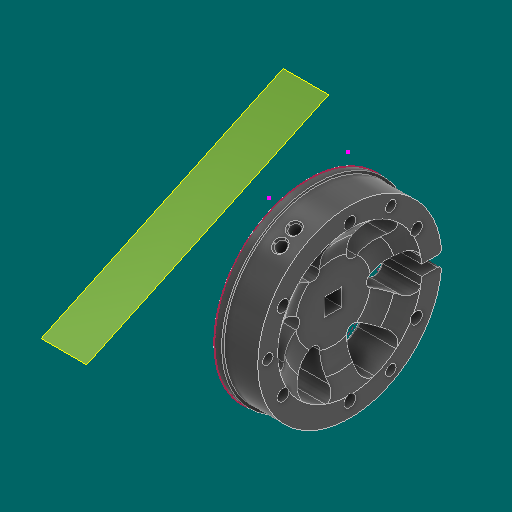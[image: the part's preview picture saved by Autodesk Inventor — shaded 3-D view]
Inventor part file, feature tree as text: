
AUTODESK INVENTOR PART (.ipt)
format: ipt  version: 2023.1 (Build 271208000, 208)  size: 545,792 bytes
history: native  units: in
note: dims shown in document units (in); Inventor stores cm internally (conversion verified against a paired STEP export)
features: sketch x7, other x4, plane x1
ambient origin geometry x8: Origin, YZ Plane, XZ Plane, XY Plane, X Axis, Y Axis, Z Axis, Center Point
bodies: Solid1 (feature_tree)
feature tree (12):
  other  "WheelHalf.ipt"
  other  "Solid1::WheelHalf.ipt"
  other  "TaggingFeature1"
  sketch  "Sketch1"  dims[d0=0.3937in]
  sketch  "Sketch2"
  sketch  "Sketch3"
  sketch  "Sketch4"
  sketch  "Sketch5"
  sketch  "Sketch6"
  sketch  "Sketch7"
  plane  "Work Plane1"
  other  "Work Axis1"
